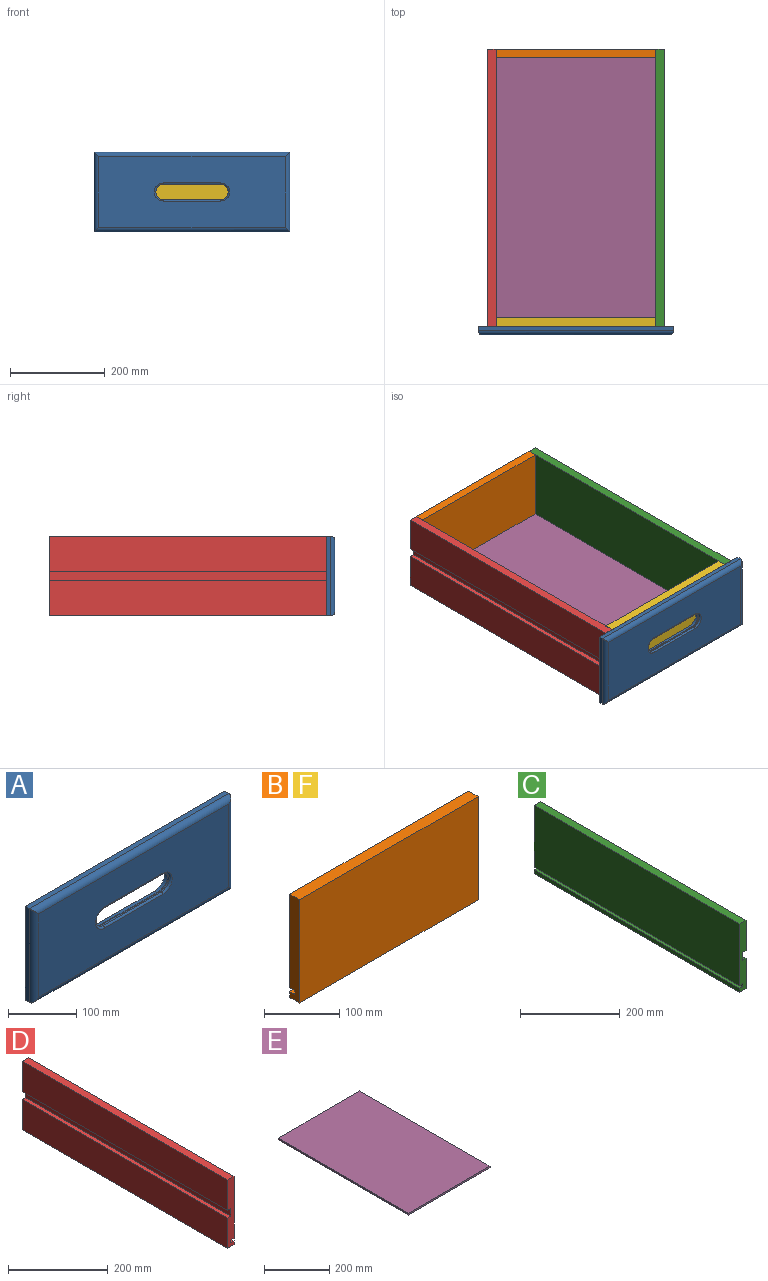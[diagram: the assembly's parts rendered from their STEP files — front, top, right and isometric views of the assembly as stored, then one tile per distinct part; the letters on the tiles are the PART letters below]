
ASSEMBLY  parts=6 mates=5
PART A: 27 faces, bbox 412.9x18.3x168.3 mm
  f0: cylinder r=15.88mm len=31.75mm, axis (0,1,0), area 120.3mm2, adj f1,f3,f17,f20
  f1: plane 120.65x2.41mm, normal (0,0,-1), area 291.1mm2, adj f0,f2,f18,f22
  f2: cylinder r=15.88mm len=31.75mm, axis (0,1,0), area 120.3mm2, adj f1,f3,f16,f21
  f3: plane 120.65x2.41mm, normal (0,0,1), area 291.1mm2, adj f0,f2,f15,f19
  f4: plane 412.88x168.28mm, normal (0,1,0), area 62562.2mm2, adj f5,f7,f8,f9,f11,f12,f13,f14
  f5: plane 412.88x8.76mm, normal (0,0,1), area 3618mm2, adj f4,f8,f9,f26
  f6: plane 393.83x149.23mm, normal (0,-1,0), area 53032mm2, adj f19,f20,f21,f22,f23,f24,f25,f26
  f7: plane 412.88x8.76mm, normal (0,0,-1), area 3618mm2, adj f4,f8,f9,f23
  f8: plane 168.28x8.76mm, normal (1,0,0), area 1474.6mm2, adj f4,f5,f7,f24
  f9: plane 168.28x8.76mm, normal (-1,0,0), area 1474.6mm2, adj f4,f5,f7,f25
  f10: plane 165.1x44.45mm, normal (0,1,0), area 1177.8mm2, adj f11,f12,f13,f14,f15,f16,f17,f18
  f11: plane 120.65x9.53mm, normal (0,0,-1), area 1149.2mm2, adj f4,f10,f12,f14
  f12: cylinder r=22.23mm len=44.45mm, axis (0,1,0), area 665.1mm2, adj f4,f10,f11,f13
  f13: plane 120.65x9.53mm, normal (0,0,1), area 1149.2mm2, adj f4,f10,f12,f14
  f14: cylinder r=22.23mm len=44.45mm, axis (0,1,0), area 665.1mm2, adj f4,f10,f11,f13
  f15: cylinder r=3.17mm len=120.65mm, axis (-1,0,0), area 601.7mm2, adj f3,f10,f16,f17
  f16: torus R=19.05mm, axis (0,1,0), area 266.8mm2, adj f2,f10,f15,f18
  f17: torus R=19.05mm, axis (0,1,0), area 266.8mm2, adj f0,f10,f15,f18
  f18: cylinder r=3.17mm len=120.65mm, axis (1,0,0), area 601.7mm2, adj f1,f10,f16,f17
  f19: cylinder r=3.17mm len=120.65mm, axis (-1,0,0), area 601.7mm2, adj f3,f6,f20,f21
  f20: torus R=19.05mm, axis (0,1,0), area 266.8mm2, adj f0,f6,f19,f22
  f21: torus R=19.05mm, axis (0,1,0), area 266.8mm2, adj f2,f6,f19,f22
  f22: cylinder r=3.17mm len=120.65mm, axis (1,0,0), area 601.7mm2, adj f1,f6,f20,f21
  f23: cylinder r=9.53mm len=412.88mm, axis (1,0,0), area 6073.8mm2, adj f6,f7,f24,f25
  f24: cylinder r=9.53mm len=168.28mm, axis (0,0,1), area 2414.1mm2, adj f6,f8,f23,f26
  f25: cylinder r=9.53mm len=168.28mm, axis (0,0,-1), area 2414.1mm2, adj f6,f9,f23,f26
  f26: cylinder r=9.53mm len=412.88mm, axis (-1,0,0), area 6073.8mm2, adj f5,f6,f24,f25
PART B: 10 faces, bbox 336.6x18.3x168.3 mm
  f0: plane 336.55x152.4mm, normal (0,1,0), area 51290.2mm2, adj f1,f2,f3,f7
  f1: plane 168.28x18.29mm, normal (1,0,0), area 3016.9mm2, adj f0,f2,f4,f5,f6,f7,f8,f9
  f2: plane 336.55x18.29mm, normal (0,0,1), area 6154.8mm2, adj f0,f1,f3,f6
  f3: plane 168.28x18.29mm, normal (-1,0,0), area 3016.9mm2, adj f0,f2,f4,f5,f6,f7,f8,f9
  f4: plane 336.55x18.29mm, normal (0,0,-1), area 6154.8mm2, adj f1,f3,f5,f6
  f5: plane 336.55x9.53mm, normal (0,1,0), area 3205.6mm2, adj f1,f3,f4,f9
  f6: plane 336.55x168.28mm, normal (0,-1,0), area 56633mm2, adj f1,f2,f3,f4
  f7: plane 336.55x9.53mm, normal (0,0,-1), area 3205.6mm2, adj f0,f1,f3,f8
  f8: plane 336.55x6.35mm, normal (0,1,0), area 2137.1mm2, adj f1,f3,f7,f9
  f9: plane 336.55x9.53mm, normal (0,0,1), area 3205.6mm2, adj f1,f3,f5,f8
PART C: 14 faces, bbox 18.3x584.2x168.3 mm
  f0: plane 168.28x18.29mm, normal (0,1,0), area 2835.5mm2, adj f1,f2,f3,f4,f5,f6,f7,f8
  f1: plane 584.2x9.53mm, normal (-1,0,0), area 5564.5mm2, adj f0,f2,f12,f13
  f2: plane 584.2x9.53mm, normal (0,0,1), area 5564.5mm2, adj f0,f1,f3,f13
  f3: plane 584.2x6.35mm, normal (-1,0,0), area 3709.7mm2, adj f0,f2,f4,f13
  f4: plane 584.2x9.53mm, normal (0,0,-1), area 5564.5mm2, adj f0,f3,f5,f13
  f5: plane 584.2x152.4mm, normal (-1,0,0), area 89032.1mm2, adj f0,f4,f6,f13
  f6: plane 584.2x18.29mm, normal (0,0,1), area 10683.8mm2, adj f0,f5,f7,f13
  f7: plane 584.2x74.61mm, normal (1,0,0), area 43588.6mm2, adj f0,f6,f8,f13
  f8: plane 584.2x9.53mm, normal (0,0,-1), area 5564.5mm2, adj f0,f7,f9,f13
  f9: plane 584.2x19.05mm, normal (1,0,0), area 11129mm2, adj f0,f8,f10,f13
  f10: plane 584.2x9.53mm, normal (0,0,1), area 5564.5mm2, adj f0,f9,f11,f13
  f11: plane 584.2x74.61mm, normal (1,0,0), area 43588.6mm2, adj f0,f10,f12,f13
  f12: plane 584.2x18.29mm, normal (0,0,-1), area 10683.8mm2, adj f0,f1,f11,f13
  f13: plane 168.28x18.29mm, normal (0,-1,0), area 2835.5mm2, adj f1,f2,f3,f4,f5,f6,f7,f8
PART D: 14 faces, bbox 18.3x584.2x168.3 mm
  f0: plane 168.28x18.29mm, normal (0,1,0), area 2835.5mm2, adj f1,f2,f3,f4,f5,f6,f7,f8
  f1: plane 584.2x9.53mm, normal (1,0,0), area 5564.5mm2, adj f0,f2,f12,f13
  f2: plane 584.2x9.53mm, normal (0,0,1), area 5564.5mm2, adj f0,f1,f3,f13
  f3: plane 584.2x6.35mm, normal (1,0,0), area 3709.7mm2, adj f0,f2,f4,f13
  f4: plane 584.2x9.53mm, normal (0,0,-1), area 5564.5mm2, adj f0,f3,f5,f13
  f5: plane 584.2x152.4mm, normal (1,0,0), area 89032.1mm2, adj f0,f4,f6,f13
  f6: plane 584.2x18.29mm, normal (0,0,1), area 10683.8mm2, adj f0,f5,f7,f13
  f7: plane 584.2x74.61mm, normal (-1,0,0), area 43588.6mm2, adj f0,f6,f8,f13
  f8: plane 584.2x9.53mm, normal (0,0,-1), area 5564.5mm2, adj f0,f7,f9,f13
  f9: plane 584.2x19.05mm, normal (-1,0,0), area 11129mm2, adj f0,f8,f10,f13
  f10: plane 584.2x9.53mm, normal (0,0,1), area 5564.5mm2, adj f0,f9,f11,f13
  f11: plane 584.2x74.61mm, normal (-1,0,0), area 43588.6mm2, adj f0,f10,f12,f13
  f12: plane 584.2x18.29mm, normal (0,0,-1), area 10683.8mm2, adj f0,f1,f11,f13
  f13: plane 168.28x18.29mm, normal (0,-1,0), area 2835.5mm2, adj f1,f2,f3,f4,f5,f6,f7,f8
PART E: 6 faces, bbox 355.6x566.7x6.4 mm
  f0: plane 355.6x6.35mm, normal (0,1,0), area 2258.1mm2, adj f1,f3,f4,f5
  f1: plane 566.67x355.6mm, normal (0,0,1), area 201509.3mm2, adj f0,f2,f4,f5
  f2: plane 355.6x6.35mm, normal (0,-1,0), area 2258.1mm2, adj f1,f3,f4,f5
  f3: plane 566.67x355.6mm, normal (0,0,-1), area 201509.3mm2, adj f0,f2,f4,f5
  f4: plane 566.67x6.35mm, normal (1,0,0), area 3598.4mm2, adj f0,f1,f2,f3
  f5: plane 566.67x6.35mm, normal (-1,0,0), area 3598.4mm2, adj f0,f1,f2,f3
PART F: same geometry as B
PLACE A t=(22.48,-31.07,76.23)mm
PLACE B rot(axis=(0,0,1),180deg) t=(22.48,553.13,76.23)mm
PLACE C t=(22.48,-31.07,76.23)mm
PLACE D t=(22.48,-31.07,76.23)mm
PLACE E t=(22.48,-31.07,-98.39)mm
PLACE F t=(22.48,-31.07,76.23)mm fixed
MATE fastened D.f13 <-> F.f6  axis (0,-1,0) through (-145.8,-31.07,31.78)mm
MATE fastened C.f13 <-> F.f6  axis (0,-1,0) through (190.75,-31.07,31.78)mm
MATE fastened A.f7 <-> F.f4  axis (0,0,-1) through (22.48,-31.07,-136.49)mm
MATE fastened D.f0 <-> B.f6  axis (0,1,0) through (-145.8,553.13,31.78)mm
MATE fastened F.f8 <-> E.f2  axis (0,1,0) through (22.48,-22.31,-123.79)mm
